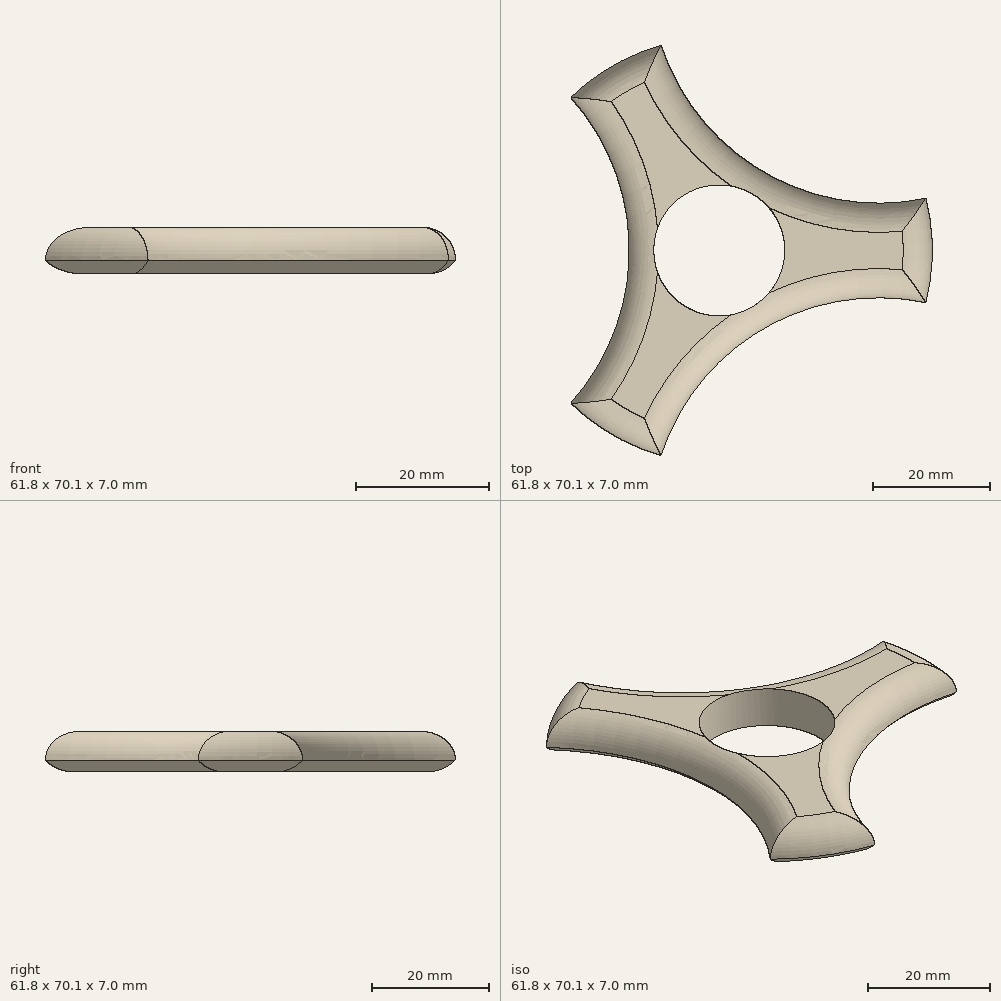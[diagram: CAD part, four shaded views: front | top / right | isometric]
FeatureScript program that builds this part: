
annotation { "Feature Type Name" : "Feature", "Feature Type Description" : "" }
export const myFeature = defineFeature(function(context is Context, id is Id, definition is map)
    precondition{}
    {
        {
            var Q0;
            Q0=qCreatedBy(makeId("Top.planeOp"),FACE);
            var sketch = newSketch(context, id + "F0", { "sketchPlane" : qUnion([Q0])});
            skCircle(sketch, "E0", {"center": v(0, 0) * mm, "radius": 11.2 * mm});
            skArc(sketch, "E1", {"start": v(-9.94, 35.05) * mm, "mid": v(-18.22, 31.55) * mm, "end": v(-25.39, 26.13) * mm});
            skArc(sketch, "E2", {"start": v(-25.39, -26.13) * mm, "mid": v(-15.4, 0) * mm, "end": v(-25.39, 26.13) * mm});
            skArc(sketch, "E3.1.0", {"start": v(35.33, -8.92) * mm, "mid": v(7.7, -13.34) * mm, "end": v(-9.94, -35.05) * mm});
            skArc(sketch, "E3.2.0", {"start": v(-9.94, 35.05) * mm, "mid": v(7.7, 13.34) * mm, "end": v(35.33, 8.92) * mm});
            skArc(sketch, "E4.trimOffspring", {"start": v(-25.39, -26.13) * mm, "mid": v(-18.22, -31.55) * mm, "end": v(-9.94, -35.05) * mm});
            skArc(sketch, "E5.trimOffspring", {"start": v(35.33, -8.92) * mm, "mid": v(36.44, 0) * mm, "end": v(35.33, 8.92) * mm});
            skSolve(sketch);
        }
        {
            var Q0;
            Q0 = qSketchRegion(id + "F0", true);
            extrude(context, id + "F1", {"entities" : qUnion([Q0]), "depth" : 7 * mm, "offsetDistance" : 25 * mm});
        }
        {
            var Q0;
            Q0=makeQuery(id+"F1.opExtrude","CAP_EDGE",EDGE,{"disambiguationData":[OSD([sQuery(id+"F0.wireOp",EDGE,"E3.1.0")])],"isStart":false});
            var Q1;
            Q1=makeQuery(id+"F1.opExtrude","CAP_EDGE",EDGE,{"disambiguationData":[OSD([sQuery(id+"F0.wireOp",EDGE,"E5.trimOffspring")])],"isStart":false});
            var Q2;
            Q2=makeQuery(id+"F1.opExtrude","CAP_EDGE",EDGE,{"disambiguationData":[OSD([sQuery(id+"F0.wireOp",EDGE,"E3.2.0")])],"isStart":false});
            var Q3;
            Q3=makeQuery(id+"F1.opExtrude","CAP_EDGE",EDGE,{"disambiguationData":[OSD([sQuery(id+"F0.wireOp",EDGE,"E1")])],"isStart":false});
            var Q4;
            Q4=makeQuery(id+"F1.opExtrude","CAP_EDGE",EDGE,{"disambiguationData":[OSD([sQuery(id+"F0.wireOp",EDGE,"E2")])],"isStart":false});
            var Q5;
            Q5=makeQuery(id+"F1.opExtrude","CAP_EDGE",EDGE,{"disambiguationData":[OSD([sQuery(id+"F0.wireOp",EDGE,"E4.trimOffspring")])],"isStart":false});
            fillet(context, id + "F2", {"entities" : qUnion([Q0, Q1, Q2, Q3, Q4, Q5]), "radius" : 5 * mm, "tangentPropagation" : true, "allowEdgeOverflow" : false});
        }
        {
            var Q0;
            Q0=makeQuery(id+"F1.opExtrude","CAP_EDGE",EDGE,{"disambiguationData":[OSD([sQuery(id+"F0.wireOp",EDGE,"E3.1.0")])],"isStart":true});
            var Q1;
            Q1=makeQuery(id+"F1.opExtrude","CAP_EDGE",EDGE,{"disambiguationData":[OSD([sQuery(id+"F0.wireOp",EDGE,"E4.trimOffspring")])],"isStart":true});
            var Q2;
            Q2=makeQuery(id+"F1.opExtrude","CAP_EDGE",EDGE,{"disambiguationData":[OSD([sQuery(id+"F0.wireOp",EDGE,"E2")])],"isStart":true});
            var Q3;
            Q3=makeQuery(id+"F1.opExtrude","CAP_EDGE",EDGE,{"disambiguationData":[OSD([sQuery(id+"F0.wireOp",EDGE,"E3.2.0")])],"isStart":true});
            var Q4;
            Q4=makeQuery(id+"F1.opExtrude","CAP_EDGE",EDGE,{"disambiguationData":[OSD([sQuery(id+"F0.wireOp",EDGE,"E1")])],"isStart":true});
            var Q5;
            Q5=makeQuery(id+"F1.opExtrude","CAP_EDGE",EDGE,{"disambiguationData":[OSD([sQuery(id+"F0.wireOp",EDGE,"E5.trimOffspring")])],"isStart":true});
            fillet(context, id + "F3", {"entities" : qUnion([Q0, Q1, Q2, Q3, Q4, Q5]), "radius" : 5 * mm, "tangentPropagation" : true, "allowEdgeOverflow" : false});
        }
    });
